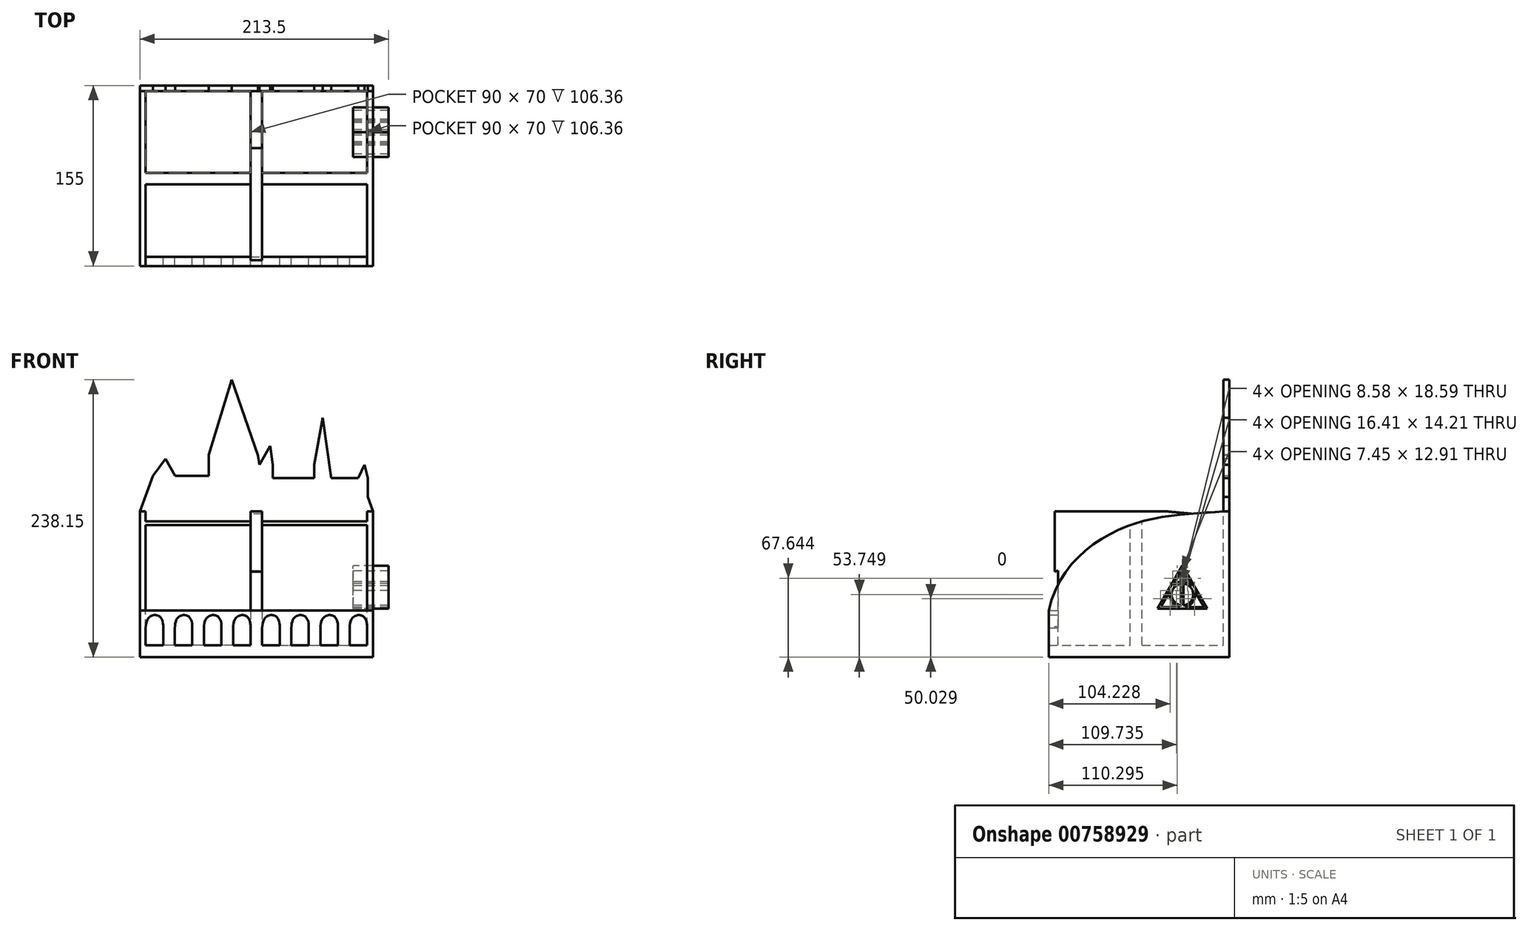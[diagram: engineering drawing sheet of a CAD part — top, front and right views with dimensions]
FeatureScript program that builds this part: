
annotation { "Feature Type Name" : "Feature", "Feature Type Description" : "" }
export const myFeature = defineFeature(function(context is Context, id is Id, definition is map)
    precondition{}
    {
        {
            var Q0;
            Q0=qCreatedBy(makeId("Front.planeOp"),FACE);
            var sketch = newSketch(context, id + "F0", { "sketchPlane" : qUnion([Q0])});
            skLineSegment(sketch, "E0", {"start": v(-120, -65.8) * mm, "end": v(80, -65.8) * mm});
            skLineSegment(sketch, "E1", {"start": v(-120, -65.8) * mm, "end": v(-120, -25.8) * mm});
            skLineSegment(sketch, "E2", {"start": v(80, -65.8) * mm, "end": v(80, -25.8) * mm});
            skLineSegment(sketch, "E3", {"start": v(-120, -25.8) * mm, "end": v(80, -25.8) * mm});
            skLineSegment(sketch, "E4", {"start": v(-115, -55.8) * mm, "end": v(-100, -55.8) * mm});
            skLineSegment(sketch, "E5", {"start": v(-90, -55.8) * mm, "end": v(-75, -55.8) * mm});
            skLineSegment(sketch, "E6", {"start": v(-65, -55.8) * mm, "end": v(-50, -55.8) * mm});
            skLineSegment(sketch, "E7", {"start": v(-40, -55.8) * mm, "end": v(-25, -55.8) * mm});
            skLineSegment(sketch, "E8", {"start": v(-15, -55.8) * mm, "end": v(0, -55.8) * mm});
            skLineSegment(sketch, "E9", {"start": v(10, -55.8) * mm, "end": v(25, -55.8) * mm});
            skLineSegment(sketch, "E10", {"start": v(35, -55.8) * mm, "end": v(50, -55.8) * mm});
            skLineSegment(sketch, "E11", {"start": v(60, -55.8) * mm, "end": v(75, -55.8) * mm});
            skLineSegment(sketch, "E12", {"start": v(-115, -55.8) * mm, "end": v(-115, -40.8) * mm});
            skLineSegment(sketch, "E13", {"start": v(-100, -55.8) * mm, "end": v(-100, -40.8) * mm});
            skLineSegment(sketch, "E14", {"start": v(-90, -55.8) * mm, "end": v(-90, -40.8) * mm});
            skLineSegment(sketch, "E15", {"start": v(-75, -55.8) * mm, "end": v(-75, -40.8) * mm});
            skLineSegment(sketch, "E16", {"start": v(-65, -55.8) * mm, "end": v(-65, -40.8) * mm});
            skLineSegment(sketch, "E17", {"start": v(-50, -55.8) * mm, "end": v(-50, -40.8) * mm});
            skLineSegment(sketch, "E18", {"start": v(-40, -55.8) * mm, "end": v(-40, -40.8) * mm});
            skLineSegment(sketch, "E19", {"start": v(-25, -55.8) * mm, "end": v(-25, -40.8) * mm});
            skLineSegment(sketch, "E20", {"start": v(-15, -55.8) * mm, "end": v(-15, -40.8) * mm});
            skLineSegment(sketch, "E21", {"start": v(0, -55.8) * mm, "end": v(0, -40.8) * mm});
            skLineSegment(sketch, "E22", {"start": v(10, -55.8) * mm, "end": v(10, -40.8) * mm});
            skLineSegment(sketch, "E23", {"start": v(25, -55.8) * mm, "end": v(25, -40.8) * mm});
            skLineSegment(sketch, "E24", {"start": v(35, -55.8) * mm, "end": v(35, -40.8) * mm});
            skLineSegment(sketch, "E25", {"start": v(50, -55.8) * mm, "end": v(50, -40.8) * mm});
            skLineSegment(sketch, "E26", {"start": v(60, -55.8) * mm, "end": v(60, -40.8) * mm});
            skLineSegment(sketch, "E27", {"start": v(75, -55.8) * mm, "end": v(75, -40.8) * mm});
            skFitSpline(sketch, "E28", {"points": [v(-115, -40.8) * mm, v(-107.07, -29.73) * mm, v(-100, -40.8) * mm], "startDerivative": vector(0.6, 51.8) * mm, "endDerivative": vector(-1.33, -52.67) * mm});
            skFitSpline(sketch, "E29", {"points": [v(-90, -40.8) * mm, v(-82.07, -29.73) * mm, v(-75, -40.8) * mm], "startDerivative": vector(0.6, 51.8) * mm, "endDerivative": vector(-1.33, -52.67) * mm});
            skFitSpline(sketch, "E30", {"points": [v(-65, -40.8) * mm, v(-57.07, -29.73) * mm, v(-50, -40.8) * mm], "startDerivative": vector(0.6, 51.8) * mm, "endDerivative": vector(-1.33, -52.67) * mm});
            skFitSpline(sketch, "E31", {"points": [v(-40, -40.8) * mm, v(-32.07, -29.73) * mm, v(-25, -40.8) * mm], "startDerivative": vector(0.6, 51.8) * mm, "endDerivative": vector(-1.33, -52.67) * mm});
            skFitSpline(sketch, "E32", {"points": [v(-15, -40.8) * mm, v(-7.07, -29.73) * mm, v(0, -40.8) * mm], "startDerivative": vector(0.6, 51.8) * mm, "endDerivative": vector(-1.33, -52.67) * mm});
            skFitSpline(sketch, "E33", {"points": [v(10, -40.8) * mm, v(17.93, -29.73) * mm, v(25, -40.8) * mm], "startDerivative": vector(0.6, 51.8) * mm, "endDerivative": vector(-1.33, -52.67) * mm});
            skFitSpline(sketch, "E34", {"points": [v(35, -40.8) * mm, v(42.93, -29.73) * mm, v(50, -40.8) * mm], "startDerivative": vector(0.6, 51.8) * mm, "endDerivative": vector(-1.33, -52.67) * mm});
            skFitSpline(sketch, "E35", {"points": [v(60, -40.8) * mm, v(67.93, -29.73) * mm, v(75, -40.8) * mm], "startDerivative": vector(0.6, 51.8) * mm, "endDerivative": vector(-1.33, -52.67) * mm});
            skSolve(sketch);
        }
        {
            var Q0;
            Q0=makeQuery(id+"F0.imprint","IMPRINT",FACE,{"disambiguationData":[TD([[makeQuery(id+"F0.imprint","IMPRINT",EDGE,{"derivedFrom":sQuery(id+"F0.wireOp",EDGE,"E0")}),1.0]])]});
            extrude(context, id + "F1", {"entities" : qUnion([Q0]), "depth" : 8 * mm, "offsetDistance" : 25 * mm});
        }
        {
            var Q0;
            Q0=makeQuery(id+"F1.opExtrude","SWEPT_FACE",FACE,{"disambiguationData":[OSD([sQuery(id+"F0.wireOp",EDGE,"E2")])]});
            var sketch = newSketch(context, id + "F2", { "sketchPlane" : qUnion([Q0])});
            skLineSegment(sketch, "E36", {"start": v(-8, -65.8) * mm, "end": v(142, -65.8) * mm});
            skLineSegment(sketch, "E37", {"start": v(142, -65.8) * mm, "end": v(142, 59.2) * mm});
            skFitSpline(sketch, "E38", {"points": [v(142, 59.2) * mm, v(58.95, 46.28) * mm, v(-8, -25.8) * mm], "startDerivative": vector(-167.04, -11.97) * mm, "endDerivative": vector(-46.18, -213.97) * mm});
            skSolve(sketch);
        }
        {
            var Q0;
            Q0=makeQuery(id+"F1.opExtrude","CAP_FACE",FACE,{"disambiguationData":[OSD([sQuery(id+"F0.wireOp",EDGE,"E0"),sQuery(id+"F0.wireOp",EDGE,"E1"),sQuery(id+"F0.wireOp",EDGE,"E2"),sQuery(id+"F0.wireOp",EDGE,"E3"),sQuery(id+"F0.wireOp",EDGE,"E4"),sQuery(id+"F0.wireOp",EDGE,"E5"),sQuery(id+"F0.wireOp",EDGE,"E6"),sQuery(id+"F0.wireOp",EDGE,"E7"),sQuery(id+"F0.wireOp",EDGE,"E8"),sQuery(id+"F0.wireOp",EDGE,"E9"),sQuery(id+"F0.wireOp",EDGE,"E10"),sQuery(id+"F0.wireOp",EDGE,"E11"),sQuery(id+"F0.wireOp",EDGE,"E12"),sQuery(id+"F0.wireOp",EDGE,"E13"),sQuery(id+"F0.wireOp",EDGE,"E14"),sQuery(id+"F0.wireOp",EDGE,"E15"),sQuery(id+"F0.wireOp",EDGE,"E16"),sQuery(id+"F0.wireOp",EDGE,"E17"),sQuery(id+"F0.wireOp",EDGE,"E18"),sQuery(id+"F0.wireOp",EDGE,"E19"),sQuery(id+"F0.wireOp",EDGE,"E20"),sQuery(id+"F0.wireOp",EDGE,"E21"),sQuery(id+"F0.wireOp",EDGE,"E22"),sQuery(id+"F0.wireOp",EDGE,"E23"),sQuery(id+"F0.wireOp",EDGE,"E24"),sQuery(id+"F0.wireOp",EDGE,"E25"),sQuery(id+"F0.wireOp",EDGE,"E26"),sQuery(id+"F0.wireOp",EDGE,"E27"),sQuery(id+"F0.wireOp",EDGE,"E28"),sQuery(id+"F0.wireOp",EDGE,"E29"),sQuery(id+"F0.wireOp",EDGE,"E30"),sQuery(id+"F0.wireOp",EDGE,"E31"),sQuery(id+"F0.wireOp",EDGE,"E32"),sQuery(id+"F0.wireOp",EDGE,"E33"),sQuery(id+"F0.wireOp",EDGE,"E34"),sQuery(id+"F0.wireOp",EDGE,"E35")])],"isStart":true});
            cPlane(context, id + "F3", {"entities" : qUnion([Q0]), "cplaneType" : CPlaneType.OFFSET, "offset" : 142 * mm, "width" : 150 * mm, "height" : 150 * mm});
        }
        {
            var Q0;
            Q0=qCreatedBy(id+"F3.planeOp",FACE);
            var sketch = newSketch(context, id + "F4", { "sketchPlane" : qUnion([Q0])});
            skPoint(sketch, "E39.0", {"position": v(-80, 59.2) * mm});
            skPoint(sketch, "E40.0", {"position": v(-80, -65.8) * mm});
            skPoint(sketch, "E41", {"position": v(120, 59.2) * mm});
            skPoint(sketch, "E42", {"position": v(120, -65.8) * mm});
            skLineSegment(sketch, "E43", {"start": v(-80, 59.2) * mm, "end": v(-80, -65.8) * mm});
            skLineSegment(sketch, "E44", {"start": v(-80, -65.8) * mm, "end": v(120, -65.8) * mm});
            skLineSegment(sketch, "E45", {"start": v(120, -65.8) * mm, "end": v(120, 59.2) * mm});
            skLineSegment(sketch, "E46", {"start": v(-80, 59.2) * mm, "end": v(-75.6, 71.64) * mm});
            skLineSegment(sketch, "E47", {"start": v(-75.6, 71.64) * mm, "end": v(-75.6, 87.92) * mm});
            skLineSegment(sketch, "E48", {"start": v(-75.6, 87.92) * mm, "end": v(-72.68, 99.19) * mm});
            skLineSegment(sketch, "E49", {"start": v(-72.68, 99.19) * mm, "end": v(-67.26, 87.92) * mm});
            skLineSegment(sketch, "E50", {"start": v(-67.26, 87.92) * mm, "end": v(-44.24, 87.92) * mm});
            skLineSegment(sketch, "E51", {"start": v(-44.24, 87.92) * mm, "end": v(-36.93, 139.5) * mm});
            skLineSegment(sketch, "E52", {"start": v(-36.93, 139.5) * mm, "end": v(-29.61, 99.19) * mm});
            skLineSegment(sketch, "E53", {"start": v(-29.61, 99.19) * mm, "end": v(-29.61, 87.92) * mm});
            skLineSegment(sketch, "E54", {"start": v(-29.61, 87.92) * mm, "end": v(5.9, 87.92) * mm});
            skLineSegment(sketch, "E55", {"start": v(5.9, 87.92) * mm, "end": v(5.9, 99.19) * mm});
            skLineSegment(sketch, "E56", {"start": v(5.9, 99.19) * mm, "end": v(8.21, 115.44) * mm});
            skLineSegment(sketch, "E57", {"start": v(8.21, 115.44) * mm, "end": v(17.42, 99.19) * mm});
            skLineSegment(sketch, "E58", {"start": v(17.42, 99.19) * mm, "end": v(18.57, 107.31) * mm});
            skPoint(sketch, "E58.endSnap0", {"position": v(12.82, 107.31) * mm});
            skLineSegment(sketch, "E59", {"start": v(18.57, 107.31) * mm, "end": v(41.03, 172.35) * mm});
            skLineSegment(sketch, "E60", {"start": v(41.03, 172.35) * mm, "end": v(60.84, 107.7) * mm});
            skLineSegment(sketch, "E61", {"start": v(60.84, 107.7) * mm, "end": v(60.84, 89.66) * mm});
            skLineSegment(sketch, "E62", {"start": v(60.84, 89.66) * mm, "end": v(89.78, 89.66) * mm});
            skLineSegment(sketch, "E63", {"start": v(89.78, 89.66) * mm, "end": v(98.17, 104.34) * mm});
            skLineSegment(sketch, "E64", {"start": v(98.17, 104.34) * mm, "end": v(108.65, 89.66) * mm});
            skLineSegment(sketch, "E65", {"start": v(108.65, 89.66) * mm, "end": v(120, 59.2) * mm});
            skSolve(sketch);
        }
        {
            var Q0;
            Q0=makeQuery(id+"F1.opExtrude","SWEPT_FACE",FACE,{"disambiguationData":[OSD([sQuery(id+"F0.wireOp",EDGE,"E1")])]});
            var sketch = newSketch(context, id + "F5", { "sketchPlane" : qUnion([Q0])});
            skPoint(sketch, "E66.0", {"position": v(-142, 59.2) * mm});
            skPoint(sketch, "E67.0", {"position": v(-142, -65.8) * mm});
            skLineSegment(sketch, "E68", {"start": v(-142, 59.2) * mm, "end": v(-142, -65.8) * mm});
            skLineSegment(sketch, "E69", {"start": v(-142, -65.8) * mm, "end": v(0, -65.8) * mm});
            skLineSegment(sketch, "E70", {"start": v(0, -65.8) * mm, "end": v(0, -25.8) * mm});
            skLineSegment(sketch, "E71", {"start": v(0, -25.8) * mm, "end": v(8, -25.8) * mm});
            skFitSpline(sketch, "E72.MirrorCS", {"points": [v(-142, 59.2) * mm, v(-58.95, 46.28) * mm, v(8, -25.8) * mm], "startDerivative": vector(167.04, -11.97) * mm, "endDerivative": vector(46.18, -213.97) * mm});
            skSolve(sketch);
        }
        {
            var Q0;
            Q0=makeQuery(id+"F1.opExtrude","SWEPT_FACE",FACE,{"disambiguationData":[OSD([sQuery(id+"F0.wireOp",EDGE,"E0")])]});
            var sketch = newSketch(context, id + "F6", { "sketchPlane" : qUnion([Q0])});
            skPoint(sketch, "E73.0", {"position": v(-120, 8) * mm});
            skPoint(sketch, "E74.0", {"position": v(-120, -142) * mm});
            skPoint(sketch, "E75.0", {"position": v(80, -142) * mm});
            skPoint(sketch, "E76.0", {"position": v(80, 8) * mm});
            skLineSegment(sketch, "E77.bottom", {"start": v(-120, 8) * mm, "end": v(80, 8) * mm});
            skLineSegment(sketch, "E77.top", {"start": v(-120, -142) * mm, "end": v(80, -142) * mm});
            skLineSegment(sketch, "E77.left", {"start": v(-120, 8) * mm, "end": v(-120, -142) * mm});
            skLineSegment(sketch, "E77.right", {"start": v(80, 8) * mm, "end": v(80, -142) * mm});
            skSolve(sketch);
        }
        {
            var Q0;
            {var subQ0=sQuery(id+"F6.wireOp",EDGE,"E77.top");Q0=makeQuery(id+"F6.imprint","IMPRINT",FACE,{"disambiguationData":[TD([[makeQuery(id+"F6.imprint","IMPRINT",EDGE,{"derivedFrom":subQ0}),1.0]])]});}
            extrude(context, id + "F7", {"entities" : qUnion([Q0]), "operationType" : NewBodyOperationType.ADD, "oppositeDirection" : true, "depth" : 10 * mm, "offsetDistance" : 25 * mm});
        }
        {
            var Q0;
            {var subQ1=sQuery(id+"F2.wireOp",EDGE,"E37");Q0=makeQuery(id+"F2.imprint","IMPRINT",FACE,{"disambiguationData":[TD([[makeQuery(id+"F2.imprint","IMPRINT",EDGE,{"derivedFrom":subQ1}),1.0]])]});}
            extrude(context, id + "F8", {"entities" : qUnion([Q0]), "operationType" : NewBodyOperationType.ADD, "oppositeDirection" : true, "depth" : 5 * mm, "offsetDistance" : 25 * mm});
        }
        {
            var Q0;
            Q0=makeQuery(id+"F5.imprint","IMPRINT",FACE,{"disambiguationData":[TD([[makeQuery(id+"F5.imprint","IMPRINT",EDGE,{"derivedFrom":sQuery(id+"F5.wireOp",EDGE,"E68")}),1.0]])]});
            extrude(context, id + "F9", {"entities" : qUnion([Q0]), "operationType" : NewBodyOperationType.ADD, "oppositeDirection" : true, "depth" : 5 * mm, "offsetDistance" : 25 * mm});
        }
        {
            var Q0;
            Q0=makeQuery(id+"F4.imprint","IMPRINT",FACE,{"disambiguationData":[TD([[makeQuery(id+"F4.imprint","IMPRINT",EDGE,{"derivedFrom":sQuery(id+"F4.wireOp",EDGE,"E43")}),1.0]])]});
            extrude(context, id + "F10", {"entities" : qUnion([Q0]), "operationType" : NewBodyOperationType.ADD, "depth" : 5 * mm, "offsetDistance" : 25 * mm});
        }
        {
            var Q0;
            Q0=makeQuery(id+"F10.opExtrude","CAP_FACE",FACE,{"disambiguationData":[OSD([sQuery(id+"F4.wireOp",EDGE,"E43"),sQuery(id+"F4.wireOp",EDGE,"E44"),sQuery(id+"F4.wireOp",EDGE,"E45"),sQuery(id+"F4.wireOp",EDGE,"E46"),sQuery(id+"F4.wireOp",EDGE,"E47"),sQuery(id+"F4.wireOp",EDGE,"E48"),sQuery(id+"F4.wireOp",EDGE,"E49"),sQuery(id+"F4.wireOp",EDGE,"E50"),sQuery(id+"F4.wireOp",EDGE,"E51"),sQuery(id+"F4.wireOp",EDGE,"E52"),sQuery(id+"F4.wireOp",EDGE,"E53"),sQuery(id+"F4.wireOp",EDGE,"E54"),sQuery(id+"F4.wireOp",EDGE,"E55"),sQuery(id+"F4.wireOp",EDGE,"E56"),sQuery(id+"F4.wireOp",EDGE,"E57"),sQuery(id+"F4.wireOp",EDGE,"E58"),sQuery(id+"F4.wireOp",EDGE,"E59"),sQuery(id+"F4.wireOp",EDGE,"E60"),sQuery(id+"F4.wireOp",EDGE,"E61"),sQuery(id+"F4.wireOp",EDGE,"E62"),sQuery(id+"F4.wireOp",EDGE,"E63"),sQuery(id+"F4.wireOp",EDGE,"E64"),sQuery(id+"F4.wireOp",EDGE,"E65")])],"isStart":true});
            var sketch = newSketch(context, id + "F11", { "sketchPlane" : qUnion([Q0])});
            skLineSegment(sketch, "E78", {"start": v(-115, -55.8) * mm, "end": v(-25, -55.8) * mm});
            skLineSegment(sketch, "E79.bottom", {"start": v(-25, -55.8) * mm, "end": v(-15, -55.8) * mm});
            skLineSegment(sketch, "E79.top", {"start": v(-25, 59.2) * mm, "end": v(-15, 59.2) * mm});
            skLineSegment(sketch, "E79.left", {"start": v(-25, -55.8) * mm, "end": v(-25, 59.2) * mm});
            skLineSegment(sketch, "E79.right", {"start": v(-15, -55.8) * mm, "end": v(-15, 59.2) * mm});
            skSolve(sketch);
        }
        {
            var Q0;
            Q0=makeQuery(id+"F9.boolean.opBoolean","MERGE",FACE,{"derivedFrom":[makeQuery(id+"F1.opExtrude","SWEPT_FACE",FACE,{"disambiguationData":[OSD([sQuery(id+"F0.wireOp",EDGE,"E12")])]}),makeQuery(id+"F9.opExtrude","CAP_FACE",FACE,{"disambiguationData":[OSD([sQuery(id+"F5.wireOp",EDGE,"E68"),sQuery(id+"F5.wireOp",EDGE,"E69"),sQuery(id+"F5.wireOp",EDGE,"E70"),sQuery(id+"F5.wireOp",EDGE,"E71"),sQuery(id+"F5.wireOp",EDGE,"E72.MirrorCS")])],"isStart":false})]});
            var sketch = newSketch(context, id + "F12", { "sketchPlane" : qUnion([Q0])});
            skLineSegment(sketch, "E80", {"start": v(-8, -55.8) * mm, "end": v(62, -55.8) * mm});
            skLineSegment(sketch, "E81.bottom", {"start": v(62, -55.8) * mm, "end": v(72, -55.8) * mm});
            skLineSegment(sketch, "E81.top", {"start": v(62, 90.16) * mm, "end": v(72, 90.16) * mm});
            skLineSegment(sketch, "E81.left", {"start": v(62, -55.8) * mm, "end": v(62, 90.16) * mm});
            skLineSegment(sketch, "E81.right", {"start": v(72, -55.8) * mm, "end": v(72, 90.16) * mm});
            skSolve(sketch);
        }
        {
            var Q0;
            {var subQ0=sQuery(id+"F12.wireOp",EDGE,"E81.bottom");Q0=makeQuery(id+"F12.imprint","IMPRINT",FACE,{"disambiguationData":[TD([[makeQuery(id+"F12.imprint","IMPRINT",EDGE,{"derivedFrom":subQ0}),1.0]])]});}
            extrude(context, id + "F13", {"entities" : qUnion([Q0]), "operationType" : NewBodyOperationType.ADD, "depth" : 90 * mm, "offsetDistance" : 25 * mm});
        }
        {
            var Q0;
            Q0=makeQuery(id+"F8.boolean.opBoolean","MERGE",FACE,{"derivedFrom":[makeQuery(id+"F1.opExtrude","SWEPT_FACE",FACE,{"disambiguationData":[OSD([sQuery(id+"F0.wireOp",EDGE,"E27")])]}),makeQuery(id+"F8.opExtrude","CAP_FACE",FACE,{"disambiguationData":[OSD([sQuery(id+"F0.wireOp",EDGE,"E2"),sQuery(id+"F0.wireOp",EDGE,"E3"),sQuery(id+"F2.wireOp",EDGE,"E36"),sQuery(id+"F2.wireOp",EDGE,"E37"),sQuery(id+"F2.wireOp",EDGE,"E38")])],"isStart":false})]});
            var sketch = newSketch(context, id + "F14", { "sketchPlane" : qUnion([Q0])});
            skLineSegment(sketch, "E82", {"start": v(-142, -55.8) * mm, "end": v(-72, -55.8) * mm});
            skLineSegment(sketch, "E83.bottom", {"start": v(-72, -55.8) * mm, "end": v(-62, -55.8) * mm});
            skLineSegment(sketch, "E83.top", {"start": v(-72, 77.76) * mm, "end": v(-62, 77.76) * mm});
            skLineSegment(sketch, "E83.left", {"start": v(-72, -55.8) * mm, "end": v(-72, 77.76) * mm});
            skLineSegment(sketch, "E83.right", {"start": v(-62, -55.8) * mm, "end": v(-62, 77.76) * mm});
            skSolve(sketch);
        }
        {
            var Q0;
            {var subQ0=sQuery(id+"F14.wireOp",EDGE,"E83.bottom");Q0=makeQuery(id+"F14.imprint","IMPRINT",FACE,{"disambiguationData":[TD([[makeQuery(id+"F14.imprint","IMPRINT",EDGE,{"derivedFrom":subQ0}),-1.0]])]});}
            extrude(context, id + "F15", {"entities" : qUnion([Q0]), "operationType" : NewBodyOperationType.ADD, "depth" : 90 * mm, "offsetDistance" : 25 * mm});
        }
        {
            var Q0;
            Q0=makeQuery(id+"F11.imprint","IMPRINT",FACE,{"disambiguationData":[TD([[makeQuery(id+"F11.imprint","IMPRINT",EDGE,{"derivedFrom":sQuery(id+"F11.wireOp",EDGE,"E79.bottom")}),1.0]])]});
            extrude(context, id + "F16", {"entities" : qUnion([Q0]), "operationType" : NewBodyOperationType.ADD, "depth" : 145 * mm, "offsetDistance" : 25 * mm});
        }
        {
            var Q0;
            Q0=makeQuery(id+"F16.boolean.opBoolean","MERGE",FACE,{"derivedFrom":[makeQuery(id+"F1.opExtrude","SWEPT_FACE",FACE,{"disambiguationData":[OSD([sQuery(id+"F0.wireOp",EDGE,"E20")])]}),makeQuery(id+"F16.opExtrude","SWEPT_FACE",FACE,{"disambiguationData":[OSD([sQuery(id+"F11.wireOp",EDGE,"E79.right")])]})]});
            var sketch = newSketch(context, id + "F17", { "sketchPlane" : qUnion([Q0])});
            skFitSpline(sketch, "E84.0", {"points": [v(142, 59.2) * mm, v(115.26, 57.28) * mm, v(55.74, 56.51) * mm, v(0, 11.26) * mm, v(-8, -25.8) * mm]});
            skLineSegment(sketch, "E85.0", {"start": v(-3, 59.2) * mm, "end": v(142, 59.2) * mm});
            skLineSegment(sketch, "E86", {"start": v(-3, 59.2) * mm, "end": v(-3, -9.9) * mm});
            skSolve(sketch);
        }
        {
            var Q0;
            {var subQ0=sQuery(id+"F17.wireOp",EDGE,"E85.0");Q0=makeQuery(id+"F17.imprint","IMPRINT",FACE,{"disambiguationData":[TD([[makeQuery(id+"F17.imprint","IMPRINT",EDGE,{"derivedFrom":subQ0}),-1.0]])]});}
            extrude(context, id + "F18", {"entities" : qUnion([Q0]), "operationType" : NewBodyOperationType.REMOVE, "oppositeDirection" : true, "depth" : 51 * mm, "offsetDistance" : 25 * mm});
        }
        {
            var Q0;
            {var subQ22=sQuery(id+"F0.wireOp",EDGE,"E20");var subQ33=sQuery(id+"F0.wireOp",EDGE,"E3");var subQ37=sQuery(id+"F11.wireOp",EDGE,"E79.right");Q0=makeQuery(id+"F18.boolean.opBoolean","SPLIT",FACE,{"disambiguationData":[TD([makeQuery(id+"F1.opExtrude","SWEPT_FACE",FACE,{"disambiguationData":[OSD([subQ33])]})])],"derivedFrom":makeQuery(id+"F16.boolean.opBoolean","MERGE",FACE,{"derivedFrom":[makeQuery(id+"F1.opExtrude","SWEPT_FACE",FACE,{"disambiguationData":[OSD([subQ22])]}),makeQuery(id+"F16.opExtrude","SWEPT_FACE",FACE,{"disambiguationData":[OSD([subQ37])]})]})});}
            var sketch = newSketch(context, id + "F19", { "sketchPlane" : qUnion([Q0])});
            skLineSegment(sketch, "E87", {"start": v(0, -25.8) * mm, "end": v(-3, -25.8) * mm});
            skLineSegment(sketch, "E88", {"start": v(-3, -25.8) * mm, "end": v(-3, -9.9) * mm});
            skLineSegment(sketch, "E89", {"start": v(0, -25.8) * mm, "end": v(0, 8.53) * mm});
            skLineSegment(sketch, "E90", {"start": v(0, 8.53) * mm, "end": v(-3, 7.58) * mm});
            skLineSegment(sketch, "E91", {"start": v(-3, 7.58) * mm, "end": v(-3, -9.9) * mm});
            skSolve(sketch);
        }
        {
            var Q0;
            {var subQ0=sQuery(id+"F19.wireOp",EDGE,"E87");Q0=makeQuery(id+"F19.imprint","IMPRINT",FACE,{"disambiguationData":[TD([[makeQuery(id+"F19.imprint","IMPRINT",EDGE,{"derivedFrom":subQ0}),-1.0]])]});}
            extrude(context, id + "F20", {"entities" : qUnion([Q0]), "operationType" : NewBodyOperationType.REMOVE, "oppositeDirection" : true, "depth" : 25 * mm, "offsetDistance" : 25 * mm});
        }
        {
            var Q0;
            {var subQ0=sQuery(id+"F0.wireOp",EDGE,"E2");Q0=makeQuery(id+"F10.boolean.opBoolean","MERGE",FACE,{"derivedFrom":[makeQuery(id+"F8.boolean.opBoolean","MERGE",FACE,{"derivedFrom":[makeQuery(id+"F7.boolean.opBoolean","MERGE",FACE,{"derivedFrom":[makeQuery(id+"F1.opExtrude","SWEPT_FACE",FACE,{"disambiguationData":[OSD([subQ0])]}),makeQuery(id+"F7.opExtrude","SWEPT_FACE",FACE,{"disambiguationData":[OSD([sQuery(id+"F6.wireOp",EDGE,"E77.right")])]})]}),makeQuery(id+"F8.opExtrude","CAP_FACE",FACE,{"disambiguationData":[OSD([subQ0,sQuery(id+"F0.wireOp",EDGE,"E3"),sQuery(id+"F2.wireOp",EDGE,"E36"),sQuery(id+"F2.wireOp",EDGE,"E37"),sQuery(id+"F2.wireOp",EDGE,"E38")])],"isStart":true})]}),makeQuery(id+"F10.opExtrude","SWEPT_FACE",FACE,{"disambiguationData":[OSD([sQuery(id+"F4.wireOp",EDGE,"E43")])]})]});}
            cPlane(context, id + "F21", {"entities" : qUnion([Q0]), "cplaneType" : CPlaneType.OFFSET, "offset" : 0 * mm, "width" : 150 * mm, "height" : 150 * mm});
        }
        {
            var Q0;
            Q0=qCreatedBy(id+"F21.planeOp",FACE);
            var sketch = newSketch(context, id + "F22", { "sketchPlane" : qUnion([Q0])});
            skLineSegment(sketch, "E92", {"start": v(28.04, -45.75) * mm, "end": v(44.45, -17.33) * mm});
            skLineSegment(sketch, "E93", {"start": v(67.04, 16.6) * mm, "end": v(81.95, -9.22) * mm});
            skLineSegment(sketch, "E94", {"start": v(28.04, -45.75) * mm, "end": v(60.86, -45.75) * mm});
            skPoint(sketch, "E95.0", {"position": v(69.5, -65.8) * mm});
            skLineSegment(sketch, "E96.0", {"start": v(22.85, -48.75) * mm, "end": v(65.54, 25.2) * mm});
            skLineSegment(sketch, "E96.1", {"start": v(22.85, -48.75) * mm, "end": v(108.24, -48.75) * mm});
            skLineSegment(sketch, "E96.2", {"start": v(65.54, 25.2) * mm, "end": v(108.24, -48.75) * mm});
            skLineSegment(sketch, "E97.left", {"start": v(64.04, 16.6) * mm, "end": v(64.04, -2) * mm});
            skLineSegment(sketch, "E97.right", {"start": v(67.04, 16.6) * mm, "end": v(67.04, -2) * mm});
            skPoint(sketch, "E97.middle", {"position": v(65.54, -13.28) * mm});
            skArc(sketch, "E98.0", {"start": v(64.04, -5.51) * mm, "mid": v(46.9, -24.1) * mm, "end": v(64.04, -42.7) * mm});
            skLineSegment(sketch, "E99.trimOffspring", {"start": v(64.04, -5.51) * mm, "end": v(64.04, -42.7) * mm});
            skLineSegment(sketch, "E100.trimOffspring", {"start": v(67.04, -5.51) * mm, "end": v(67.04, -42.7) * mm});
            skPoint(sketch, "E101.orphan", {"position": v(64.04, 19.2) * mm});
            skPoint(sketch, "E102.orphan", {"position": v(67.04, 19.2) * mm});
            skPoint(sketch, "E103.orphan", {"position": v(65.54, 19.2) * mm});
            skArc(sketch, "E104.trimOffspring", {"start": v(67.04, -42.7) * mm, "mid": v(84.2, -24.1) * mm, "end": v(67.04, -5.51) * mm});
            skLineSegment(sketch, "E105.trimOffspring", {"start": v(70.22, -45.75) * mm, "end": v(103.04, -45.75) * mm});
            skLineSegment(sketch, "E106.trimOffspring", {"start": v(64.04, -45.7) * mm, "end": v(64.04, -45.75) * mm});
            skLineSegment(sketch, "E107.trimOffspring", {"start": v(67.04, -45.7) * mm, "end": v(67.04, -45.75) * mm});
            skArc(sketch, "E108.0", {"start": v(70.22, -45.75) * mm, "mid": v(84.73, -35.18) * mm, "end": v(86.63, -17.33) * mm});
            skArc(sketch, "E109.0", {"start": v(64.01, -2) * mm, "mid": v(55.87, -4.17) * mm, "end": v(49.13, -9.22) * mm});
            skLineSegment(sketch, "E110.trimOffspring", {"start": v(49.13, -9.22) * mm, "end": v(64.04, 16.6) * mm});
            skArc(sketch, "E111.trimOffspring", {"start": v(44.45, -17.33) * mm, "mid": v(46.36, -35.18) * mm, "end": v(60.86, -45.75) * mm});
            skLineSegment(sketch, "E112", {"start": v(64.01, -2) * mm, "end": v(64.04, -2) * mm});
            skLineSegment(sketch, "E113", {"start": v(67.08, -2) * mm, "end": v(67.04, -2) * mm});
            skArc(sketch, "E114.trimOffspring", {"start": v(81.95, -9.22) * mm, "mid": v(75.22, -4.17) * mm, "end": v(67.08, -2) * mm});
            skLineSegment(sketch, "E115.trimOffspring", {"start": v(86.63, -17.33) * mm, "end": v(103.04, -45.75) * mm});
            skSolve(sketch);
        }
        {
            var Q0;
            Q0=qSketchRegion(id+"F22",true);
            extrude(context, id + "F23", {"entities" : qUnion([Q0]), "depth" : 61 * mm, "offsetDistance" : 25 * mm});
        }
        {
            var Q0;
            Q0=makeQuery(id+"F23.opExtrude","SWEPT_BODY",BODY,{"disambiguationData":[OSD([sQuery(id+"F22.wireOp",EDGE,"E92"),sQuery(id+"F22.wireOp",EDGE,"E93"),sQuery(id+"F22.wireOp",EDGE,"E94"),sQuery(id+"F22.wireOp",EDGE,"E96.0"),sQuery(id+"F22.wireOp",EDGE,"E96.1"),sQuery(id+"F22.wireOp",EDGE,"E96.2"),sQuery(id+"F22.wireOp",EDGE,"E97.left"),sQuery(id+"F22.wireOp",EDGE,"E97.right"),sQuery(id+"F22.wireOp",EDGE,"E98.0"),sQuery(id+"F22.wireOp",EDGE,"E99.trimOffspring"),sQuery(id+"F22.wireOp",EDGE,"E100.trimOffspring"),sQuery(id+"F22.wireOp",EDGE,"E104.trimOffspring"),sQuery(id+"F22.wireOp",EDGE,"E105.trimOffspring"),sQuery(id+"F22.wireOp",EDGE,"E108.0"),sQuery(id+"F22.wireOp",EDGE,"E109.0"),sQuery(id+"F22.wireOp",EDGE,"E110.trimOffspring"),sQuery(id+"F22.wireOp",EDGE,"E111.trimOffspring"),sQuery(id+"F22.wireOp",EDGE,"E112"),sQuery(id+"F22.wireOp",EDGE,"E113"),sQuery(id+"F22.wireOp",EDGE,"E114.trimOffspring"),sQuery(id+"F22.wireOp",EDGE,"E115.trimOffspring")])]});
            var Q1;
            Q1=qCreatedBy(makeId("Origin.pointOp"),VERTEX);
            transform(context, id + "F24", {"entities" : qUnion([Q0]), "transformType" : TransformType.SCALE_UNIFORMLY, "scale" : 0.5, "scalePoint" : qUnion([Q1]), "makeCopy" : false});
        }
        {
            var Q0;
            Q0=makeQuery(id+"F23.opExtrude","SWEPT_BODY",BODY,{"disambiguationData":[OSD([sQuery(id+"F22.wireOp",EDGE,"E92"),sQuery(id+"F22.wireOp",EDGE,"E93"),sQuery(id+"F22.wireOp",EDGE,"E94"),sQuery(id+"F22.wireOp",EDGE,"E96.0"),sQuery(id+"F22.wireOp",EDGE,"E96.1"),sQuery(id+"F22.wireOp",EDGE,"E96.2"),sQuery(id+"F22.wireOp",EDGE,"E97.left"),sQuery(id+"F22.wireOp",EDGE,"E97.right"),sQuery(id+"F22.wireOp",EDGE,"E98.0"),sQuery(id+"F22.wireOp",EDGE,"E99.trimOffspring"),sQuery(id+"F22.wireOp",EDGE,"E100.trimOffspring"),sQuery(id+"F22.wireOp",EDGE,"E104.trimOffspring"),sQuery(id+"F22.wireOp",EDGE,"E105.trimOffspring"),sQuery(id+"F22.wireOp",EDGE,"E108.0"),sQuery(id+"F22.wireOp",EDGE,"E109.0"),sQuery(id+"F22.wireOp",EDGE,"E110.trimOffspring"),sQuery(id+"F22.wireOp",EDGE,"E111.trimOffspring"),sQuery(id+"F22.wireOp",EDGE,"E112"),sQuery(id+"F22.wireOp",EDGE,"E113"),sQuery(id+"F22.wireOp",EDGE,"E114.trimOffspring"),sQuery(id+"F22.wireOp",EDGE,"E115.trimOffspring")])]});
            transform(context, id + "F25", {"entities" : qUnion([Q0]), "transformType" : TransformType.TRANSLATION_3D, "dx" : 23 * mm, "dy" : 74 * mm, "dz" : 0 * mm, "makeCopy" : false});
        }
        {
            var Q0;
            {var subQ0=sQuery(id+"F0.wireOp",EDGE,"E2");Q0=makeQuery(id+"F10.boolean.opBoolean","MERGE",FACE,{"derivedFrom":[makeQuery(id+"F8.boolean.opBoolean","MERGE",FACE,{"derivedFrom":[makeQuery(id+"F7.boolean.opBoolean","MERGE",FACE,{"derivedFrom":[makeQuery(id+"F1.opExtrude","SWEPT_FACE",FACE,{"disambiguationData":[OSD([subQ0])]}),makeQuery(id+"F7.opExtrude","SWEPT_FACE",FACE,{"disambiguationData":[OSD([sQuery(id+"F6.wireOp",EDGE,"E77.right")])]})]}),makeQuery(id+"F8.opExtrude","CAP_FACE",FACE,{"disambiguationData":[OSD([subQ0,sQuery(id+"F0.wireOp",EDGE,"E3"),sQuery(id+"F2.wireOp",EDGE,"E36"),sQuery(id+"F2.wireOp",EDGE,"E37"),sQuery(id+"F2.wireOp",EDGE,"E38")])],"isStart":true})]}),makeQuery(id+"F10.opExtrude","SWEPT_FACE",FACE,{"disambiguationData":[OSD([sQuery(id+"F4.wireOp",EDGE,"E43")])]})]});}
            cPlane(context, id + "F26", {"entities" : qUnion([Q0]), "cplaneType" : CPlaneType.OFFSET, "offset" : 0 * mm, "width" : 150 * mm, "height" : 150 * mm});
        }
        {
            var Q0;
            Q0=qCreatedBy(id+"F26.planeOp",FACE);
            var sketch = newSketch(context, id + "F27", { "sketchPlane" : qUnion([Q0])});
            skLineSegment(sketch, "E116.0.0", {"start": v(128.12, -24.38) * mm, "end": v(106.77, 12.6) * mm});
            skLineSegment(sketch, "E116.0.1", {"start": v(106.77, 12.6) * mm, "end": v(85.42, -24.38) * mm});
            skLineSegment(sketch, "E116.0.2", {"start": v(85.42, -24.38) * mm, "end": v(128.12, -24.38) * mm});
            skLineSegment(sketch, "E117.0", {"start": v(98.57, -4.61) * mm, "end": v(106.02, 8.3) * mm});
            skArc(sketch, "E118.0", {"start": v(106, -1) * mm, "mid": v(101.94, -2.09) * mm, "end": v(98.57, -4.61) * mm});
            skLineSegment(sketch, "E119.0", {"start": v(106.02, 8.3) * mm, "end": v(106.02, -1) * mm});
            skArc(sketch, "E120.0", {"start": v(114.98, -4.61) * mm, "mid": v(111.6, -2.09) * mm, "end": v(107.54, -1) * mm});
            skLineSegment(sketch, "E121.0", {"start": v(107.52, 8.3) * mm, "end": v(107.52, -1) * mm});
            skLineSegment(sketch, "E122.0", {"start": v(107.52, 8.3) * mm, "end": v(114.98, -4.61) * mm});
            skArc(sketch, "E123.0", {"start": v(107.52, -21.35) * mm, "mid": v(116.1, -12.05) * mm, "end": v(107.52, -2.76) * mm});
            skLineSegment(sketch, "E124.0", {"start": v(107.52, -2.76) * mm, "end": v(107.52, -21.35) * mm});
            skLineSegment(sketch, "E125.0", {"start": v(106.02, -2.76) * mm, "end": v(106.02, -21.35) * mm});
            skArc(sketch, "E126.0", {"start": v(106.02, -2.76) * mm, "mid": v(97.45, -12.05) * mm, "end": v(106.02, -21.35) * mm});
            skLineSegment(sketch, "E127.0", {"start": v(109.11, -22.88) * mm, "end": v(125.52, -22.88) * mm});
            skLineSegment(sketch, "E128.0", {"start": v(117.32, -8.66) * mm, "end": v(125.52, -22.88) * mm});
            skArc(sketch, "E129.0", {"start": v(109.11, -22.88) * mm, "mid": v(116.36, -17.59) * mm, "end": v(117.32, -8.66) * mm});
            skLineSegment(sketch, "E130.0", {"start": v(88.02, -22.88) * mm, "end": v(104.43, -22.88) * mm});
            skArc(sketch, "E131.0", {"start": v(96.23, -8.66) * mm, "mid": v(97.18, -17.59) * mm, "end": v(104.43, -22.88) * mm});
            skLineSegment(sketch, "E132.0", {"start": v(88.02, -22.88) * mm, "end": v(96.23, -8.66) * mm});
            skLineSegment(sketch, "E133", {"start": v(106, -1) * mm, "end": v(106.02, -1) * mm});
            skLineSegment(sketch, "E134", {"start": v(107.52, -1) * mm, "end": v(107.54, -1) * mm});
            skSolve(sketch);
        }
        {
            var Q0;
            Q0=makeQuery(id+"F27.imprint","IMPRINT",FACE,{"disambiguationData":[TD([[makeQuery(id+"F27.imprint","IMPRINT",EDGE,{"derivedFrom":sQuery(id+"F27.wireOp",EDGE,"E130.0")}),1.0]])]});
            var Q1;
            Q1=makeQuery(id+"F27.imprint","IMPRINT",FACE,{"disambiguationData":[TD([[makeQuery(id+"F27.imprint","IMPRINT",EDGE,{"derivedFrom":sQuery(id+"F27.wireOp",EDGE,"E125.0")}),-1.0]])]});
            var Q2;
            Q2=makeQuery(id+"F27.imprint","IMPRINT",FACE,{"disambiguationData":[TD([[makeQuery(id+"F27.imprint","IMPRINT",EDGE,{"derivedFrom":sQuery(id+"F27.wireOp",EDGE,"E123.0")}),1.0]])]});
            var Q3;
            Q3=makeQuery(id+"F27.imprint","IMPRINT",FACE,{"disambiguationData":[TD([[makeQuery(id+"F27.imprint","IMPRINT",EDGE,{"derivedFrom":sQuery(id+"F27.wireOp",EDGE,"E120.0")}),-1.0]])]});
            var Q4;
            Q4=makeQuery(id+"F27.imprint","IMPRINT",FACE,{"disambiguationData":[TD([[makeQuery(id+"F27.imprint","IMPRINT",EDGE,{"derivedFrom":sQuery(id+"F27.wireOp",EDGE,"E117.0")}),-1.0]])]});
            var Q5;
            Q5=makeQuery(id+"F27.imprint","IMPRINT",FACE,{"disambiguationData":[TD([[makeQuery(id+"F27.imprint","IMPRINT",EDGE,{"derivedFrom":sQuery(id+"F27.wireOp",EDGE,"E127.0")}),1.0]])]});
            extrude(context, id + "F28", {"entities" : qUnion([Q0, Q1, Q2, Q3, Q4, Q5]), "operationType" : NewBodyOperationType.REMOVE, "oppositeDirection" : true, "depth" : 25 * mm, "offsetDistance" : 25 * mm});
        }
    });
